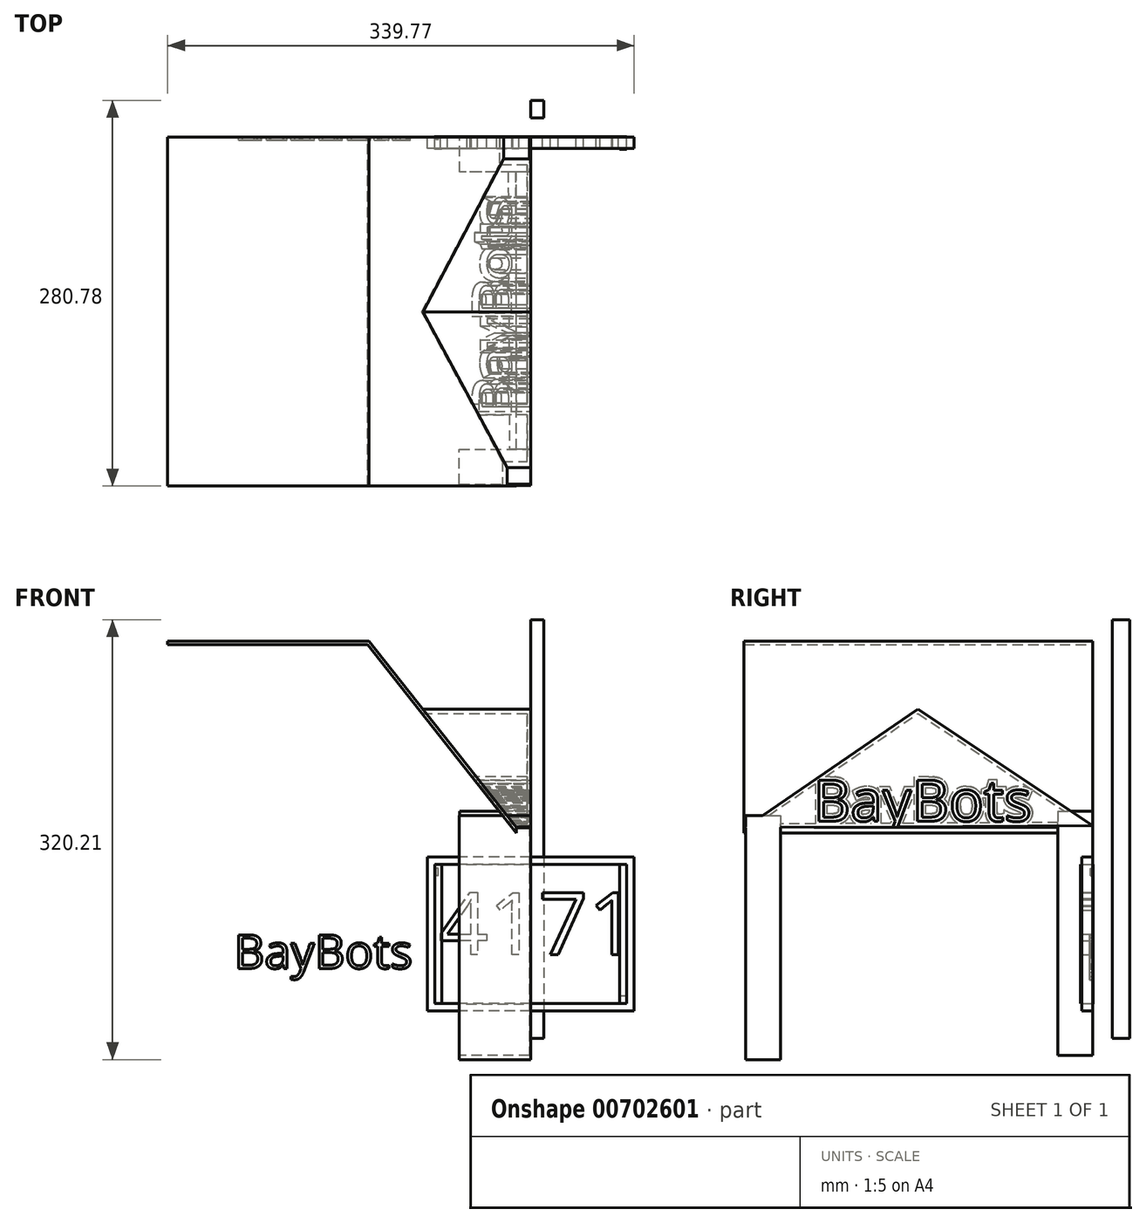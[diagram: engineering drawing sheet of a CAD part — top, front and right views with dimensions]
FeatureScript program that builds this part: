
annotation { "Feature Type Name" : "Feature", "Feature Type Description" : "" }
export const myFeature = defineFeature(function(context is Context, id is Id, definition is map)
    precondition{}
    {
        {
            var Q0;
            Q0=qCreatedBy(makeId("Front.planeOp"),FACE);
            var sketch = newSketch(context, id + "F0", { "sketchPlane" : qUnion([Q0])});
            skLineSegment(sketch, "E0.bottom", {"start": v(-264.39, 213.08) * mm, "end": v(-117.63, 213.08) * mm});
            skLineSegment(sketch, "E0.top", {"start": v(-264.39, -142.52) * mm, "end": v(-10.39, -142.52) * mm});
            skLineSegment(sketch, "E0.left", {"start": v(-264.39, 213.08) * mm, "end": v(-264.39, -142.52) * mm});
            skLineSegment(sketch, "E0.right", {"start": v(-10.39, 77.67) * mm, "end": v(-10.39, -142.52) * mm});
            skLineSegment(sketch, "E1", {"start": v(-10.39, 77.67) * mm, "end": v(-117.63, 213.08) * mm});
            skSolve(sketch);
        }
        {
            var Q0;
            Q0 = qSketchRegion(id + "F0", true);
            extrude(context, id + "F1", {"entities" : qUnion([Q0]), "depth" : 254 * mm, "offsetDistance" : 25.4 * mm});
        }
        {
            var Q0;
            Q0=qCreatedBy(makeId("Right.planeOp"),FACE);
            var sketch = newSketch(context, id + "F2", { "sketchPlane" : qUnion([Q0])});
            skLineSegment(sketch, "E2", {"start": v(0, 78.77) * mm, "end": v(-127.35, 163.55) * mm});
            skLineSegment(sketch, "E3", {"start": v(-127.35, 163.55) * mm, "end": v(-253.72, 77.4) * mm});
            skLineSegment(sketch, "E4", {"start": v(-253.72, 77.4) * mm, "end": v(0, 78.77) * mm});
            skText(sketch, "E5", { "text": "BayBots", "fontName": "OpenSans-Regular.ttf"});
            const initialGuessF2  = {"E5": [-0.20372, 0.08209, 1, 0, 0.03023]};
            skSetInitialGuess(sketch, initialGuessF2);
            skSolve(sketch);
        }
        {
            var Q0;
            {var subQ7=sQuery(id+"F2.wireOp",EDGE,"E3");Q0=makeQuery(id+"F2.imprint","IMPRINT",FACE,{"disambiguationData":[TD([[makeQuery(id+"F2.imprint","IMPRINT",EDGE,{"derivedFrom":subQ7}),1.0]])]});}
            var Q1;
            Q1=makeQuery(id+"F2.imprint","IMPRINT",FACE,{"disambiguationData":[TD([[makeQuery(id+"F2.imprint","IMPRINT",EDGE,{"derivedFrom":sQuery(id+"F2.wireOp",EDGE,"E5.sketch_text.stroke-44")}),1.0]])]});
            var Q2;
            Q2=makeQuery(id+"F2.imprint","IMPRINT",FACE,{"disambiguationData":[TD([[makeQuery(id+"F2.imprint","IMPRINT",EDGE,{"derivedFrom":sQuery(id+"F2.wireOp",EDGE,"E5.sketch_text.stroke-18")}),1.0]])]});
            var Q3;
            Q3=makeQuery(id+"F2.imprint","IMPRINT",FACE,{"disambiguationData":[TD([[makeQuery(id+"F2.imprint","IMPRINT",EDGE,{"derivedFrom":sQuery(id+"F2.wireOp",EDGE,"E5.sketch_text.stroke-11")}),1.0]])]});
            var Q4;
            Q4=makeQuery(id+"F2.imprint","IMPRINT",FACE,{"disambiguationData":[TD([[makeQuery(id+"F2.imprint","IMPRINT",EDGE,{"derivedFrom":sQuery(id+"F2.wireOp",EDGE,"E5.sketch_text.stroke-86")}),1.0]])]});
            var Q5;
            Q5=makeQuery(id+"F2.imprint","IMPRINT",FACE,{"disambiguationData":[TD([[makeQuery(id+"F2.imprint","IMPRINT",EDGE,{"derivedFrom":sQuery(id+"F2.wireOp",EDGE,"E5.sketch_text.stroke-79")}),1.0]])]});
            var Q6;
            Q6=makeQuery(id+"F2.imprint","IMPRINT",FACE,{"disambiguationData":[TD([[makeQuery(id+"F2.imprint","IMPRINT",EDGE,{"derivedFrom":sQuery(id+"F2.wireOp",EDGE,"E5.sketch_text.stroke-102")}),1.0]])]});
            extrude(context, id + "F3", {"entities" : qUnion([Q0, Q1, Q2, Q3, Q4, Q5, Q6]), "operationType" : NewBodyOperationType.ADD, "oppositeDirection" : true, "depth" : 264.16 * mm, "offsetDistance" : 25.4 * mm});
        }
        {
            var Q0;
            Q0=makeQuery(id+"F1.opExtrude","SWEPT_FACE",FACE,{"disambiguationData":[OSD([sQuery(id+"F0.wireOp",EDGE,"E0.right")])]});
            var Q1;
            Q1=makeQuery(id+"F1.opExtrude","CAP_FACE",FACE,{"disambiguationData":[OSD([sQuery(id+"F0.wireOp",EDGE,"E0.bottom"),sQuery(id+"F0.wireOp",EDGE,"E0.top"),sQuery(id+"F0.wireOp",EDGE,"E0.left"),sQuery(id+"F0.wireOp",EDGE,"E0.right"),sQuery(id+"F0.wireOp",EDGE,"E1")])],"isStart":false});
            var Q2;
            Q2=makeQuery(id+"F1.opExtrude","SWEPT_FACE",FACE,{"disambiguationData":[OSD([sQuery(id+"F0.wireOp",EDGE,"E0.top")])]});
            var Q3;
            Q3=makeQuery(id+"F1.opExtrude","CAP_FACE",FACE,{"disambiguationData":[OSD([sQuery(id+"F0.wireOp",EDGE,"E0.bottom"),sQuery(id+"F0.wireOp",EDGE,"E0.top"),sQuery(id+"F0.wireOp",EDGE,"E0.left"),sQuery(id+"F0.wireOp",EDGE,"E0.right"),sQuery(id+"F0.wireOp",EDGE,"E1")])],"isStart":true});
            var Q4;
            Q4=makeQuery(id+"F1.opExtrude","SWEPT_FACE",FACE,{"disambiguationData":[OSD([sQuery(id+"F0.wireOp",EDGE,"E0.left")])]});
            shell(context, id + "F4", {"entities" : qUnion([Q0, Q1, Q2, Q3, Q4]), "thickness" : 2.54 * mm});
        }
        {
            var Q0;
            Q0=qCreatedBy(makeId("Front.planeOp"),FACE);
            var sketch = newSketch(context, id + "F5", { "sketchPlane" : qUnion([Q0])});
            skLineSegment(sketch, "E6.bottom", {"start": v(-1.06, 89.33) * mm, "end": v(-51.86, 89.33) * mm});
            skLineSegment(sketch, "E6.top", {"start": v(-1.06, -88.47) * mm, "end": v(-51.86, -88.47) * mm});
            skLineSegment(sketch, "E6.left", {"start": v(-1.06, 89.33) * mm, "end": v(-1.06, -88.47) * mm});
            skLineSegment(sketch, "E6.right", {"start": v(-51.86, 89.33) * mm, "end": v(-51.86, -88.47) * mm});
            skSolve(sketch);
        }
        {
            var Q0;
            Q0 = qSketchRegion(id + "F5", true);
            extrude(context, id + "F6", {"entities" : qUnion([Q0]), "operationType" : NewBodyOperationType.ADD, "depth" : 25.4 * mm, "offsetDistance" : 25.4 * mm});
        }
        {
            var Q0;
            Q0=qCreatedBy(makeId("Right.planeOp"),FACE);
            var sketch = newSketch(context, id + "F7", { "sketchPlane" : qUnion([Q0])});
            skLineSegment(sketch, "E7.bottom", {"start": v(-252.7, 86.33) * mm, "end": v(-227.3, 86.33) * mm});
            skLineSegment(sketch, "E7.top", {"start": v(-252.7, -91.47) * mm, "end": v(-227.3, -91.47) * mm});
            skLineSegment(sketch, "E7.left", {"start": v(-252.7, 86.33) * mm, "end": v(-252.7, -91.47) * mm});
            skLineSegment(sketch, "E7.right", {"start": v(-227.3, 86.33) * mm, "end": v(-227.3, -91.47) * mm});
            skSolve(sketch);
        }
        {
            var Q0;
            Q0 = qSketchRegion(id + "F7", true);
            extrude(context, id + "F8", {"entities" : qUnion([Q0]), "operationType" : NewBodyOperationType.ADD, "oppositeDirection" : true, "depth" : 52.07 * mm, "offsetDistance" : 25.4 * mm});
        }
        {
            var Q0;
            Q0=qCreatedBy(makeId("Right.planeOp"),FACE);
            var sketch = newSketch(context, id + "F9", { "sketchPlane" : qUnion([Q0])});
            skLineSegment(sketch, "E8.bottom", {"start": v(14.08, 228.74) * mm, "end": v(26.78, 228.74) * mm});
            skLineSegment(sketch, "E8.top", {"start": v(14.08, -76.06) * mm, "end": v(26.78, -76.06) * mm});
            skLineSegment(sketch, "E8.left", {"start": v(14.08, 228.74) * mm, "end": v(14.08, -76.06) * mm});
            skLineSegment(sketch, "E8.right", {"start": v(26.78, 228.74) * mm, "end": v(26.78, -76.06) * mm});
            skSolve(sketch);
        }
        {
            var Q0;
            Q0 = qSketchRegion(id + "F9", true);
            extrude(context, id + "F10", {"entities" : qUnion([Q0]), "depth" : 9.65 * mm, "offsetDistance" : 25.4 * mm});
        }
        {
            var Q0;
            Q0=qCreatedBy(makeId("Front.planeOp"),FACE);
            var sketch = newSketch(context, id + "F11", { "sketchPlane" : qUnion([Q0])});
            skLineSegment(sketch, "E9.bottom", {"start": v(69.84, 50.7) * mm, "end": v(-69.84, 50.7) * mm});
            skLineSegment(sketch, "E9.top", {"start": v(69.84, -50.7) * mm, "end": v(-69.84, -50.7) * mm});
            skLineSegment(sketch, "E9.left", {"start": v(69.84, 50.7) * mm, "end": v(69.84, -50.7) * mm});
            skLineSegment(sketch, "E9.right", {"start": v(-69.84, 50.7) * mm, "end": v(-69.84, -50.7) * mm});
            skPoint(sketch, "E9.middle", {"position": v(0, 0) * mm});
            skLineSegment(sketch, "E10.bottom", {"start": v(75.38, 56) * mm, "end": v(-75.38, 56) * mm});
            skLineSegment(sketch, "E10.top", {"start": v(75.38, -56) * mm, "end": v(-75.38, -56) * mm});
            skLineSegment(sketch, "E10.left", {"start": v(75.38, 56) * mm, "end": v(75.38, -56) * mm});
            skLineSegment(sketch, "E10.right", {"start": v(-75.38, 56) * mm, "end": v(-75.38, -56) * mm});
            skText(sketch, "E11", { "text": "4171", "fontName": "OpenSans-Regular.ttf"});
            const initialGuessF11  = {"E11": [-0.06699, -0.01519, 1, 0, 0.04567]};
            skSetInitialGuess(sketch, initialGuessF11);
            skSolve(sketch);
        }
        {
            var Q0;
            Q0=makeQuery(id+"F11.imprint","IMPRINT",FACE,{"disambiguationData":[TD([[makeQuery(id+"F11.imprint","IMPRINT",EDGE,{"derivedFrom":sQuery(id+"F11.wireOp",EDGE,"E11.sketch_text.stroke-0")}),-1.0]])]});
            var Q1;
            Q1=makeQuery(id+"F11.imprint","IMPRINT",FACE,{"disambiguationData":[TD([[makeQuery(id+"F11.imprint","IMPRINT",EDGE,{"derivedFrom":sQuery(id+"F11.wireOp",EDGE,"E11.sketch_text.stroke-17")}),-1.0]])]});
            var Q2;
            Q2=makeQuery(id+"F11.imprint","IMPRINT",FACE,{"disambiguationData":[TD([[makeQuery(id+"F11.imprint","IMPRINT",EDGE,{"derivedFrom":sQuery(id+"F11.wireOp",EDGE,"E11.sketch_text.stroke-26")}),-1.0]])]});
            var Q3;
            Q3=makeQuery(id+"F11.imprint","IMPRINT",FACE,{"disambiguationData":[TD([[makeQuery(id+"F11.imprint","IMPRINT",EDGE,{"derivedFrom":sQuery(id+"F11.wireOp",EDGE,"E11.sketch_text.stroke-33")}),-1.0]])]});
            var Q4;
            Q4=makeQuery(id+"F11.imprint","IMPRINT",FACE,{"disambiguationData":[TD([[makeQuery(id+"F11.imprint","IMPRINT",EDGE,{"derivedFrom":sQuery(id+"F11.wireOp",EDGE,"E9.bottom")}),-1.0]])]});
            extrude(context, id + "F12", {"entities" : qUnion([Q0, Q1, Q2, Q3, Q4]), "depth" : 8.13 * mm, "offsetDistance" : 25.4 * mm});
        }
        {
            var Q0;
            Q0=qCreatedBy(makeId("Front.planeOp"),FACE);
            var sketch = newSketch(context, id + "F13", { "sketchPlane" : qUnion([Q0])});
            skLineSegment(sketch, "E12.bottom", {"start": v(-70.01, 50.8) * mm, "end": v(70.01, 50.8) * mm});
            skLineSegment(sketch, "E12.top", {"start": v(-70.01, -50.8) * mm, "end": v(64.85, -50.8) * mm});
            skLineSegment(sketch, "E12.left", {"start": v(-70.01, 50.8) * mm, "end": v(-70.01, -50.8) * mm});
            skLineSegment(sketch, "E12.right", {"start": v(70.01, 50.8) * mm, "end": v(70.01, -45.18) * mm});
            skPoint(sketch, "E12.middle", {"position": v(0, 0) * mm});
            skLineSegment(sketch, "E13", {"start": v(70.01, -45.18) * mm, "end": v(64.85, -45.18) * mm});
            skLineSegment(sketch, "E14", {"start": v(64.85, -45.18) * mm, "end": v(64.85, -50.8) * mm});
            skPoint(sketch, "E15.orphan", {"position": v(70.01, -50.8) * mm});
            skSolve(sketch);
        }
        {
            var Q0;
            Q0 = qSketchRegion(id + "F13", true);
            extrude(context, id + "F14", {"entities" : qUnion([Q0]), "oppositeDirection" : true, "depth" : 0.25 * mm, "offsetDistance" : 25.4 * mm});
        }
        {
            var Q0;
            Q0=qCreatedBy(makeId("Front.planeOp"),FACE);
            var sketch = newSketch(context, id + "F15", { "sketchPlane" : qUnion([Q0])});
            skLineSegment(sketch, "E16.bottom", {"start": v(-67.37, 42.54) * mm, "end": v(-69.02, 42.54) * mm});
            skLineSegment(sketch, "E16.top", {"start": v(-67.37, 47.74) * mm, "end": v(-69.02, 47.74) * mm});
            skLineSegment(sketch, "E16.left", {"start": v(-67.37, 42.54) * mm, "end": v(-67.37, 47.74) * mm});
            skLineSegment(sketch, "E16.right", {"start": v(-69.02, 42.54) * mm, "end": v(-69.02, 47.74) * mm});
            skPoint(sketch, "E16.middle", {"position": v(-68.2, 45.14) * mm});
            skSolve(sketch);
        }
        {
            var Q0;
            Q0 = qSketchRegion(id + "F15", true);
            extrude(context, id + "F16", {"entities" : qUnion([Q0]), "depth" : 1.78 * mm, "offsetDistance" : 25.4 * mm});
        }
        {
            var Q0;
            Q0=qCreatedBy(makeId("Front.planeOp"),FACE);
            var sketch = newSketch(context, id + "F17", { "sketchPlane" : qUnion([Q0])});
            skText(sketch, "E17", { "text": "BayBots", "fontName": "OpenSans-Regular.ttf"});
            const initialGuessF17  = {"E17": [-0.21607, -0.02512, 1, 0, 0.02469]};
            skSetInitialGuess(sketch, initialGuessF17);
            skSolve(sketch);
        }
        {
            var Q0;
            Q0 = qSketchRegion(id + "F17", true);
            extrude(context, id + "F18", {"entities" : qUnion([Q0]), "operationType" : NewBodyOperationType.ADD, "depth" : 2.3 * mm, "offsetDistance" : 25.4 * mm});
        }
        {
            var Q0;
            Q0=makeQuery(id+"F12.opExtrude","CAP_FACE",FACE,{"disambiguationData":[OSD([sQuery(id+"F11.wireOp",EDGE,"E9.bottom"),sQuery(id+"F11.wireOp",EDGE,"E9.top"),sQuery(id+"F11.wireOp",EDGE,"E9.left"),sQuery(id+"F11.wireOp",EDGE,"E9.right"),sQuery(id+"F11.wireOp",EDGE,"E10.bottom"),sQuery(id+"F11.wireOp",EDGE,"E10.top"),sQuery(id+"F11.wireOp",EDGE,"E10.left"),sQuery(id+"F11.wireOp",EDGE,"E10.right")])],"isStart":false});
            var sketch = newSketch(context, id + "F19", { "sketchPlane" : qUnion([Q0])});
            skLineSegment(sketch, "E18", {"start": v(-64.76, 50.7) * mm, "end": v(-64.76, -50.7) * mm});
            skLineSegment(sketch, "E19", {"start": v(-64.76, -50.7) * mm, "end": v(-69.84, -50.7) * mm});
            skLineSegment(sketch, "E20", {"start": v(-69.84, -50.7) * mm, "end": v(-69.84, 50.7) * mm});
            skLineSegment(sketch, "E21", {"start": v(-69.84, 50.7) * mm, "end": v(-64.76, 50.7) * mm});
            skLineSegment(sketch, "E22", {"start": v(69.84, 50.7) * mm, "end": v(64.76, 50.7) * mm});
            skLineSegment(sketch, "E23", {"start": v(64.76, 50.7) * mm, "end": v(64.76, -50.7) * mm});
            skLineSegment(sketch, "E24", {"start": v(64.76, -50.7) * mm, "end": v(69.84, -50.7) * mm});
            skLineSegment(sketch, "E25", {"start": v(69.84, -50.7) * mm, "end": v(69.84, 50.7) * mm});
            skSolve(sketch);
        }
        {
            var Q0;
            Q0 = qSketchRegion(id + "F19", true);
            extrude(context, id + "F20", {"entities" : qUnion([Q0]), "depth" : 0.76 * mm, "offsetDistance" : 25.4 * mm});
        }
    });
